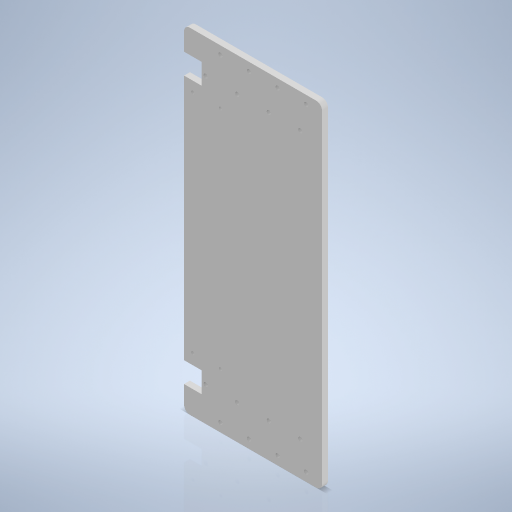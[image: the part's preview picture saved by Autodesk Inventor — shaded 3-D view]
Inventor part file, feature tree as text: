
AUTODESK INVENTOR PART (.ipt)
format: ipt  version: 2024 (Build 280153000, 153)  size: 313,344 bytes
history: native  units: mm
features: sketch x6, hole x4, extrude x2, fillet x1, plane x1, mirror x1
ambient origin geometry x8: Origin, YZ Plane, XZ Plane, XY Plane, X Axis, Y Axis, Z Axis, Center Point
bodies: Volumenkörper1 (feature_tree)
feature tree (15):
  extrude  "Extrusion1"  Depth=140.0mm
  extrude  "Extrusion2"  Depth=21.0mm
  hole  "Bohrung1"  [1 undecoded]
  fillet  "Rundung1"  Radius=24.0mm
  hole  "Bohrung2"  [1 undecoded]
  plane  "Arbeitsebene1"
  mirror  "Spiegeln1"
  hole  "Bohrung3"  [1 undecoded]
  hole  "Bohrung4"  [1 undecoded]
  sketch  "Skizze1"  dims[d0=340.0mm d1=140.0mm]
  sketch  "Skizze2"  dims[d2=6.0mm d3=0.0mm d4=21.0mm]
  sketch  "Skizze3"  dims[d5=21.0mm d6=24.0mm d7=24.0mm]
  sketch  "Skizze4"  dims[d8=18.0mm d9=6.0mm d10=0.0mm]
  sketch  "Skizze5"  dims[d11=22.0mm d12=32.0mm]
  sketch  "Skizze6"  dims[d13=32.0mm d14=32.0mm d15=4.134mm d16=10.0mm d17=4.0mm d18=2.0mm d19=90.0deg d20=8.0mm d21=0.0mm d22=6.0mm d23=26.0mm d24=16.0mm d25=29.0mm d26=29.0mm d27=29.0mm d28=4.134mm d29=10.0mm d30=4.0mm d31=2.0mm d32=90.0deg d33=8.0mm d34=0.0mm d35=0.0mm d36=114.5mm d37=114.5mm d38=3.242mm d39=8.0mm d40=4.0mm d41=2.0mm d42=90.0deg d43=8.0mm d44=0.0mm d45=19.0mm d46=114.5mm d47=114.5mm d48=3.242mm d49=8.0mm d50=4.0mm d51=2.0mm d52=90.0deg d53=8.0mm d54=0.0mm]
note: 4 required parameter values undecoded (feature->parameter linkage not recoverable at this tier; creation-order binding heuristic only, values carry confidence <= 0.55)
